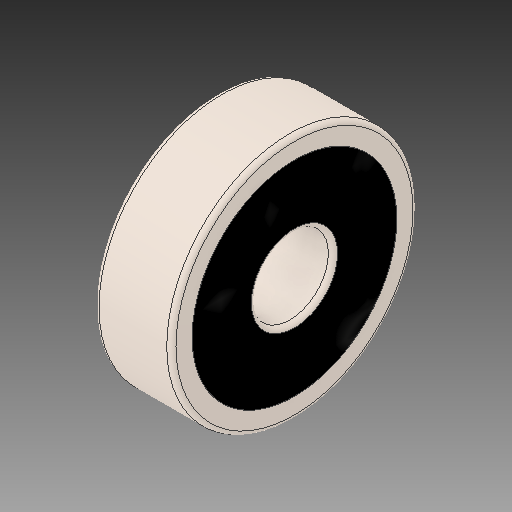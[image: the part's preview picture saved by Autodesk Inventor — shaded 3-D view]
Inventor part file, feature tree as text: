
AUTODESK INVENTOR PART (.ipt)
format: ipt  version: 2017 (Build 210142000, 142)  size: 2,300,928 bytes
history: imported  units: mm
features: other x22, sketch x2, imported_body x1
ambient origin geometry x8: Origin, YZ Plane, XZ Plane, XY Plane, X Axis, Y Axis, Z Axis, Center Point
bodies: Solid1 (imported_parasolid), Solid2 (imported_parasolid), Solid3 (imported_parasolid), Solid4 (imported_parasolid), Solid5 (imported_parasolid), Solid6 (imported_parasolid), Solid7 (imported_parasolid), Solid8 (imported_parasolid), Solid9 (imported_parasolid), Solid10 (imported_parasolid), Solid11 (imported_parasolid), Solid12 (imported_parasolid), Solid13 (imported_parasolid), Solid14 (imported_parasolid), Solid15 (imported_parasolid), Solid16 (imported_parasolid), Solid17 (imported_parasolid), Solid18 (imported_parasolid), Solid19 (imported_parasolid), Solid20 (imported_parasolid)
feature tree (25):
  other  "SKF 625_CPY.ipt"
  other  "Solid1::SKF 625_CPY.ipt"
  other  "Solid2::SKF 625_CPY.ipt"
  other  "Solid3::SKF 625_CPY.ipt"
  other  "Solid4::SKF 625_CPY.ipt"
  other  "Solid5::SKF 625_CPY.ipt"
  other  "Solid6::SKF 625_CPY.ipt"
  other  "Solid7::SKF 625_CPY.ipt"
  other  "Solid8::SKF 625_CPY.ipt"
  other  "Solid9::SKF 625_CPY.ipt"
  other  "Solid10::SKF 625_CPY.ipt"
  other  "Solid11::SKF 625_CPY.ipt"
  other  "Solid12::SKF 625_CPY.ipt"
  other  "Solid13::SKF 625_CPY.ipt"
  other  "Solid14::SKF 625_CPY.ipt"
  other  "Solid15::SKF 625_CPY.ipt"
  other  "Solid16::SKF 625_CPY.ipt"
  other  "Solid17::SKF 625_CPY.ipt"
  other  "Solid18::SKF 625_CPY.ipt"
  other  "Solid19::SKF 625_CPY.ipt"
  other  "Solid20::SKF 625_CPY.ipt"
  other  "TaggingFeature1"
  sketch  "Sketch1"  dims[d0=10.0mm]
  sketch  "Sketch2"
  imported_body  NMx_Import_Brep_tag  [imported B-rep: ~49 faces, bbox_mm=None]
